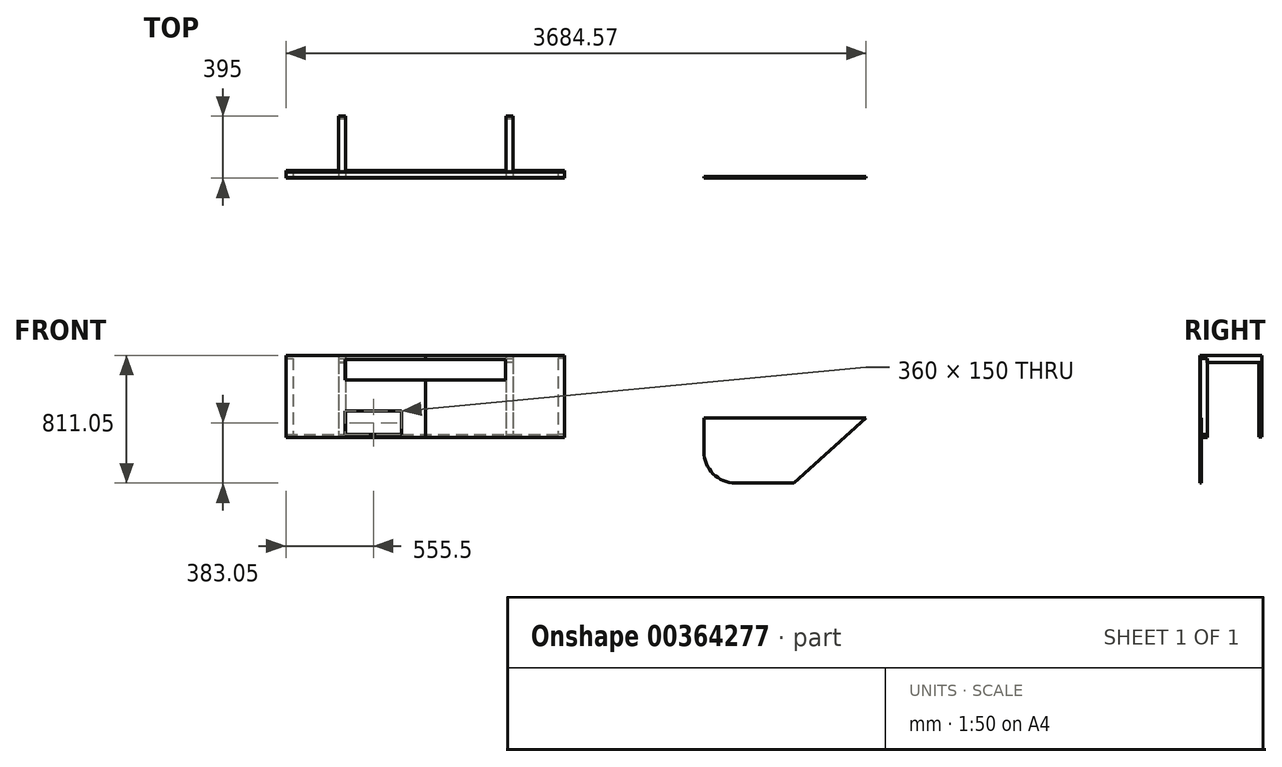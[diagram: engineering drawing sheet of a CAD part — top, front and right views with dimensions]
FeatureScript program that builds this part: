
annotation { "Feature Type Name" : "Feature", "Feature Type Description" : "" }
export const myFeature = defineFeature(function(context is Context, id is Id, definition is map)
    precondition{}
    {
        {
            var Q0;
            Q0=qCreatedBy(makeId("Front.planeOp"),FACE);
            var sketch = newSketch(context, id + "F0", { "sketchPlane" : qUnion([Q0])});
            skLineSegment(sketch, "E0.bottom", {"start": v(442.75, 261.5) * mm, "end": v(-442.75, 261.5) * mm});
            skLineSegment(sketch, "E0.top", {"start": v(442.75, -261.5) * mm, "end": v(-442.75, -261.5) * mm});
            skLineSegment(sketch, "E0.left", {"start": v(442.75, 261.5) * mm, "end": v(442.75, -261.5) * mm});
            skLineSegment(sketch, "E0.right", {"start": v(-442.75, 261.5) * mm, "end": v(-442.75, -261.5) * mm});
            skPoint(sketch, "E0.middle", {"position": v(0, 0) * mm});
            skSolve(sketch);
        }
        {
            var Q0;
            Q0 = qSketchRegion(id + "F0", true);
            extrude(context, id + "F1", {"entities" : qUnion([Q0]), "depth" : 3 * mm});
        }
        {
            var Q0;
            Q0=makeQuery(id+"F1.opExtrude","CAP_FACE",FACE,{"disambiguationData":[OSD([sQuery(id+"F0.wireOp",EDGE,"E0.bottom"),sQuery(id+"F0.wireOp",EDGE,"E0.top"),sQuery(id+"F0.wireOp",EDGE,"E0.left"),sQuery(id+"F0.wireOp",EDGE,"E0.right")])],"isStart":false});
            var sketch = newSketch(context, id + "F2", { "sketchPlane" : qUnion([Q0])});
            skLineSegment(sketch, "E1.bottom", {"start": v(442.75, 261.5) * mm, "end": v(1328.25, 261.5) * mm});
            skLineSegment(sketch, "E1.top", {"start": v(442.75, -261.5) * mm, "end": v(1328.25, -261.5) * mm});
            skLineSegment(sketch, "E1.left", {"start": v(442.75, 261.5) * mm, "end": v(442.75, -261.5) * mm});
            skLineSegment(sketch, "E1.right", {"start": v(1328.25, 261.5) * mm, "end": v(1328.25, -261.5) * mm});
            skSolve(sketch);
        }
        {
            var Q0;
            Q0 = qSketchRegion(id + "F2", true);
            extrude(context, id + "F3", {"entities" : qUnion([Q0]), "oppositeDirection" : true, "depth" : 3 * mm});
        }
        {
            var Q0;
            Q0=makeQuery(id+"F1.opExtrude","CAP_FACE",FACE,{"disambiguationData":[OSD([sQuery(id+"F0.wireOp",EDGE,"E0.bottom"),sQuery(id+"F0.wireOp",EDGE,"E0.top"),sQuery(id+"F0.wireOp",EDGE,"E0.left"),sQuery(id+"F0.wireOp",EDGE,"E0.right")])],"isStart":false});
            var sketch = newSketch(context, id + "F4", { "sketchPlane" : qUnion([Q0])});
            skLineSegment(sketch, "E2.bottom", {"start": v(952.75, 236.5) * mm, "end": v(-67.25, 236.5) * mm});
            skLineSegment(sketch, "E2.top", {"start": v(952.75, 106.5) * mm, "end": v(-67.25, 106.5) * mm});
            skLineSegment(sketch, "E2.left", {"start": v(952.75, 236.5) * mm, "end": v(952.75, 106.5) * mm});
            skLineSegment(sketch, "E2.right", {"start": v(-67.25, 236.5) * mm, "end": v(-67.25, 106.5) * mm});
            skPoint(sketch, "E2.middle", {"position": v(442.75, 171.5) * mm});
            skSolve(sketch);
        }
        {
            var Q0;
            Q0 = qSketchRegion(id + "F4", true);
            extrude(context, id + "F5", {"entities" : qUnion([Q0]), "operationType" : NewBodyOperationType.REMOVE, "oppositeDirection" : true, "depth" : 25 * mm});
        }
        {
            var Q0;
            Q0=makeQuery(id+"F1.opExtrude","CAP_FACE",FACE,{"disambiguationData":[OSD([sQuery(id+"F0.wireOp",EDGE,"E0.bottom"),sQuery(id+"F0.wireOp",EDGE,"E0.top"),sQuery(id+"F0.wireOp",EDGE,"E0.left"),sQuery(id+"F0.wireOp",EDGE,"E0.right")])],"isStart":false});
            var sketch = newSketch(context, id + "F6", { "sketchPlane" : qUnion([Q0])});
            skLineSegment(sketch, "E3.bottom", {"start": v(-67.25, -91.5) * mm, "end": v(292.75, -91.5) * mm});
            skLineSegment(sketch, "E3.top", {"start": v(-67.25, -241.5) * mm, "end": v(292.75, -241.5) * mm});
            skLineSegment(sketch, "E3.left", {"start": v(-67.25, -91.5) * mm, "end": v(-67.25, -241.5) * mm});
            skLineSegment(sketch, "E3.right", {"start": v(292.75, -91.5) * mm, "end": v(292.75, -241.5) * mm});
            skSolve(sketch);
        }
        {
            var Q0;
            Q0=makeQuery(id+"F6.imprint","IMPRINT",FACE,{"disambiguationData":[TD([[makeQuery(id+"F6.imprint","IMPRINT",EDGE,{"derivedFrom":sQuery(id+"F6.wireOp",EDGE,"E3.bottom")}),-1.0]])]});
            extrude(context, id + "F7", {"entities" : qUnion([Q0]), "operationType" : NewBodyOperationType.REMOVE, "oppositeDirection" : true, "depth" : 25 * mm});
        }
        {
            var Q0;
            Q0=makeQuery(id+"F3.opExtrude","SWEPT_FACE",FACE,{"disambiguationData":[OSD([sQuery(id+"F2.wireOp",EDGE,"E1.right")])]});
            var sketch = newSketch(context, id + "F8", { "sketchPlane" : qUnion([Q0])});
            skLineSegment(sketch, "E4.bottom", {"start": v(0, 261.5) * mm, "end": v(37, 261.5) * mm});
            skLineSegment(sketch, "E4.top", {"start": v(0, 242.5) * mm, "end": v(37, 242.5) * mm});
            skLineSegment(sketch, "E4.left", {"start": v(0, 261.5) * mm, "end": v(0, 242.5) * mm});
            skLineSegment(sketch, "E4.right", {"start": v(37, 261.5) * mm, "end": v(37, 242.5) * mm});
            skLineSegment(sketch, "E5.bottom", {"start": v(0, -261.5) * mm, "end": v(45, -261.5) * mm});
            skLineSegment(sketch, "E5.top", {"start": v(0, -241.5) * mm, "end": v(45, -241.5) * mm});
            skLineSegment(sketch, "E5.left", {"start": v(0, -261.5) * mm, "end": v(0, -241.5) * mm});
            skLineSegment(sketch, "E5.right", {"start": v(45, -261.5) * mm, "end": v(45, -241.5) * mm});
            skSolve(sketch);
        }
        {
            var Q0;
            Q0 = qSketchRegion(id + "F8", true);
            extrude(context, id + "F9", {"entities" : qUnion([Q0]), "oppositeDirection" : true, "depth" : 1771 * mm});
        }
        {
            var Q0;
            Q0=makeQuery(id+"F9.opExtrude","SWEPT_FACE",FACE,{"disambiguationData":[OSD([sQuery(id+"F8.wireOp",EDGE,"E5.top")])]});
            var sketch = newSketch(context, id + "F10", { "sketchPlane" : qUnion([Q0])});
            skLineSegment(sketch, "E6.bottom", {"start": v(-442.75, 45) * mm, "end": v(-398.75, 45) * mm});
            skLineSegment(sketch, "E6.top", {"start": v(-442.75, 1) * mm, "end": v(-398.75, 1) * mm});
            skLineSegment(sketch, "E6.left", {"start": v(-442.75, 45) * mm, "end": v(-442.75, 1) * mm});
            skLineSegment(sketch, "E6.right", {"start": v(-398.75, 45) * mm, "end": v(-398.75, 1) * mm});
            skLineSegment(sketch, "E7.bottom", {"start": v(-109.25, 45) * mm, "end": v(-65.25, 45) * mm});
            skLineSegment(sketch, "E7.top", {"start": v(-109.25, 1) * mm, "end": v(-65.25, 1) * mm});
            skLineSegment(sketch, "E7.left", {"start": v(-109.25, 45) * mm, "end": v(-109.25, 1) * mm});
            skLineSegment(sketch, "E7.right", {"start": v(-65.25, 45) * mm, "end": v(-65.25, 1) * mm});
            skLineSegment(sketch, "E8.bottom", {"start": v(954.75, 45) * mm, "end": v(998.75, 45) * mm});
            skLineSegment(sketch, "E8.top", {"start": v(954.75, 1) * mm, "end": v(998.75, 1) * mm});
            skLineSegment(sketch, "E8.left", {"start": v(954.75, 45) * mm, "end": v(954.75, 1) * mm});
            skLineSegment(sketch, "E8.right", {"start": v(998.75, 45) * mm, "end": v(998.75, 1) * mm});
            skLineSegment(sketch, "E9.bottom", {"start": v(1328.25, 45) * mm, "end": v(1284.25, 45) * mm});
            skLineSegment(sketch, "E9.top", {"start": v(1328.25, 1) * mm, "end": v(1284.25, 1) * mm});
            skLineSegment(sketch, "E9.left", {"start": v(1328.25, 45) * mm, "end": v(1328.25, 1) * mm});
            skLineSegment(sketch, "E9.right", {"start": v(1284.25, 45) * mm, "end": v(1284.25, 1) * mm});
            skSolve(sketch);
        }
        {
            var Q0;
            Q0 = qSketchRegion(id + "F10", true);
            extrude(context, id + "F11", {"entities" : qUnion([Q0]), "depth" : 484 * mm});
        }
        {
            var Q0;
            Q0=makeQuery(id+"F9.opExtrude","SWEPT_FACE",FACE,{"disambiguationData":[OSD([sQuery(id+"F8.wireOp",EDGE,"E4.right")])]});
            var sketch = newSketch(context, id + "F12", { "sketchPlane" : qUnion([Q0])});
            skLineSegment(sketch, "E10.bottom", {"start": v(-998.75, 261.5) * mm, "end": v(-953.75, 261.5) * mm});
            skLineSegment(sketch, "E10.top", {"start": v(-998.75, 216.5) * mm, "end": v(-953.75, 216.5) * mm});
            skLineSegment(sketch, "E10.left", {"start": v(-998.75, 261.5) * mm, "end": v(-998.75, 216.5) * mm});
            skLineSegment(sketch, "E10.right", {"start": v(-953.75, 261.5) * mm, "end": v(-953.75, 216.5) * mm});
            skLineSegment(sketch, "E11.bottom", {"start": v(109.25, 261.5) * mm, "end": v(64.25, 261.5) * mm});
            skLineSegment(sketch, "E11.top", {"start": v(109.25, 216.5) * mm, "end": v(64.25, 216.5) * mm});
            skLineSegment(sketch, "E11.left", {"start": v(109.25, 261.5) * mm, "end": v(109.25, 216.5) * mm});
            skLineSegment(sketch, "E11.right", {"start": v(64.25, 261.5) * mm, "end": v(64.25, 216.5) * mm});
            skSolve(sketch);
        }
        {
            var Q0;
            Q0 = qSketchRegion(id + "F12", true);
            extrude(context, id + "F13", {"entities" : qUnion([Q0]), "depth" : 355 * mm});
        }
        {
            var Q0;
            Q0=makeQuery(id+"F13.opExtrude","CAP_FACE",FACE,{"disambiguationData":[OSD([sQuery(id+"F12.wireOp",EDGE,"E10.bottom"),sQuery(id+"F12.wireOp",EDGE,"E10.top"),sQuery(id+"F12.wireOp",EDGE,"E10.left"),sQuery(id+"F12.wireOp",EDGE,"E10.right")])],"isStart":false});
            var sketch = newSketch(context, id + "F14", { "sketchPlane" : qUnion([Q0])});
            skLineSegment(sketch, "E12.bottom", {"start": v(-998.75, 216.5) * mm, "end": v(-953.75, 216.5) * mm});
            skLineSegment(sketch, "E12.top", {"start": v(-998.75, -258.5) * mm, "end": v(-953.75, -258.5) * mm});
            skLineSegment(sketch, "E12.left", {"start": v(-998.75, 216.5) * mm, "end": v(-998.75, -258.5) * mm});
            skLineSegment(sketch, "E12.right", {"start": v(-953.75, 216.5) * mm, "end": v(-953.75, -258.5) * mm});
            skLineSegment(sketch, "E13.bottom", {"start": v(64.25, 216.5) * mm, "end": v(109.25, 216.5) * mm});
            skLineSegment(sketch, "E13.top", {"start": v(64.25, -258.5) * mm, "end": v(109.25, -258.5) * mm});
            skLineSegment(sketch, "E13.left", {"start": v(64.25, 216.5) * mm, "end": v(64.25, -258.5) * mm});
            skLineSegment(sketch, "E13.right", {"start": v(109.25, 216.5) * mm, "end": v(109.25, -258.5) * mm});
            skSolve(sketch);
        }
        {
            var Q0;
            Q0 = qSketchRegion(id + "F14", true);
            extrude(context, id + "F15", {"entities" : qUnion([Q0]), "oppositeDirection" : true, "depth" : 20 * mm});
        }
        {
            var Q0;
            Q0=makeQuery(id+"F3.opExtrude","CAP_FACE",FACE,{"disambiguationData":[OSD([sQuery(id+"F2.wireOp",EDGE,"E1.bottom"),sQuery(id+"F2.wireOp",EDGE,"E1.top"),sQuery(id+"F2.wireOp",EDGE,"E1.left"),sQuery(id+"F2.wireOp",EDGE,"E1.right")])],"isStart":true});
            var sketch = newSketch(context, id + "F16", { "sketchPlane" : qUnion([Q0])});
            skLineSegment(sketch, "E14.bottom", {"start": v(2411.82, -549.55) * mm, "end": v(2783.13, -549.55) * mm});
            skLineSegment(sketch, "E14.top", {"start": v(2211.82, -136.55) * mm, "end": v(3241.82, -136.55) * mm});
            skLineSegment(sketch, "E14.left", {"start": v(2211.82, -349.55) * mm, "end": v(2211.82, -136.55) * mm});
            skPoint(sketch, "E15.visualSharp", {"position": v(2211.82, -549.55) * mm});
            skArc(sketch, "E15.filletArc", {"start": v(2211.82, -349.55) * mm, "mid": v(2270.4, -490.97) * mm, "end": v(2411.82, -549.55) * mm});
            skLineSegment(sketch, "E16", {"start": v(3241.82, -136.55) * mm, "end": v(2783.13, -549.55) * mm});
            skSolve(sketch);
        }
        {
            var Q0;
            Q0 = qSketchRegion(id + "F16", true);
            extrude(context, id + "F17", {"entities" : qUnion([Q0]), "oppositeDirection" : true, "depth" : 10 * mm});
        }
    });
